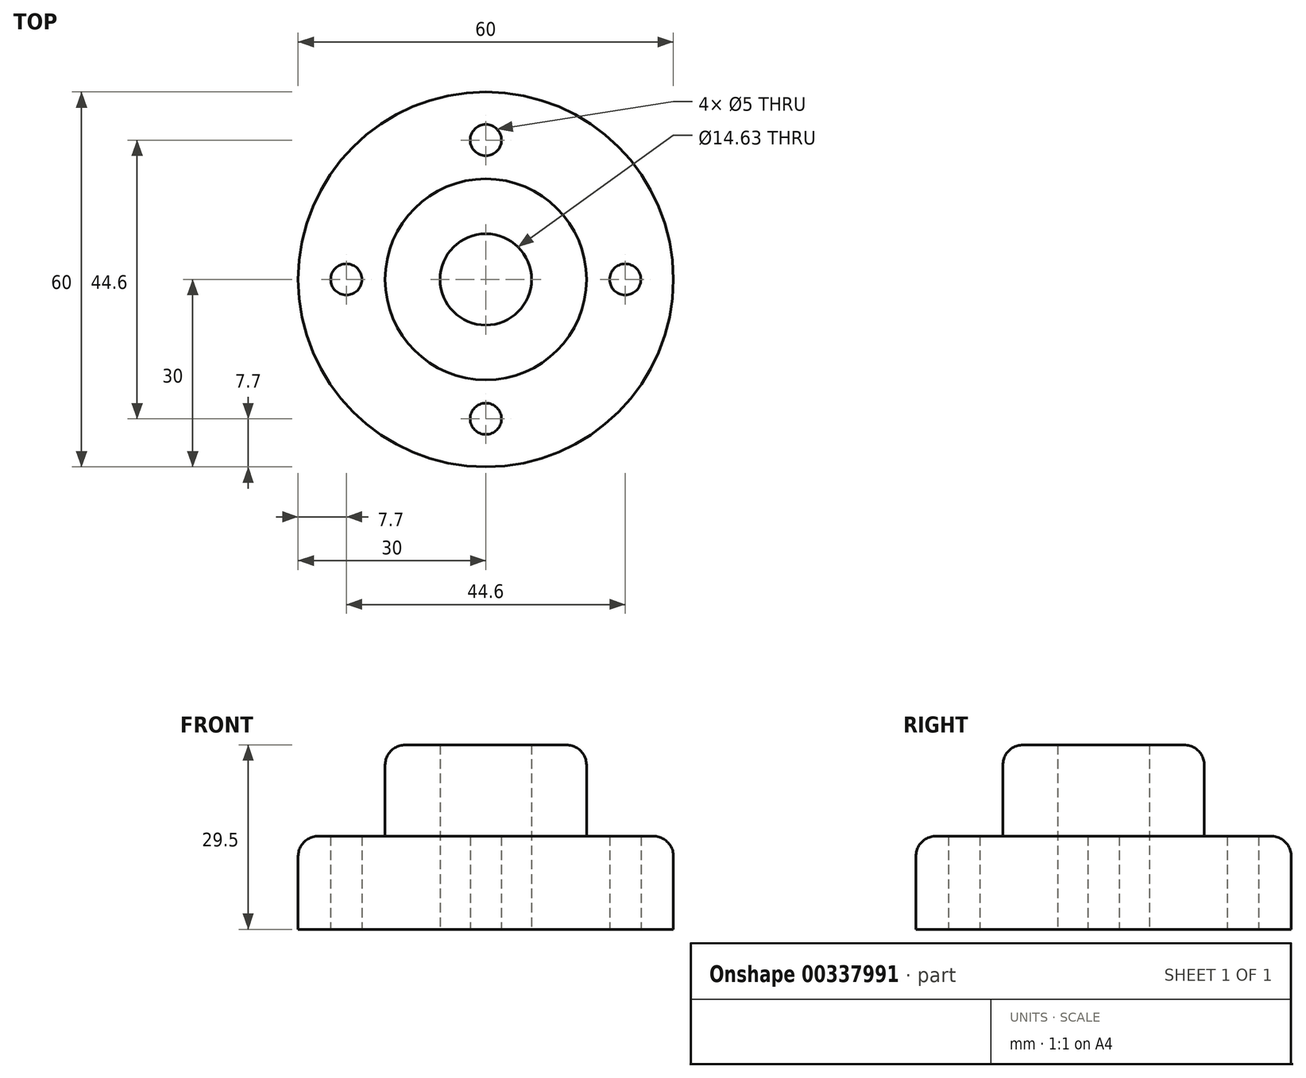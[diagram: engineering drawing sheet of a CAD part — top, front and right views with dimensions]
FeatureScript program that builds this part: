
annotation { "Feature Type Name" : "Feature", "Feature Type Description" : "" }
export const myFeature = defineFeature(function(context is Context, id is Id, definition is map)
    precondition{}
    {
        {
            var Q0;
            Q0=qCreatedBy(makeId("Top.planeOp"),FACE);
            var sketch = newSketch(context, id + "F0", { "sketchPlane" : qUnion([Q0])});
            skCircle(sketch, "E0", {"center": v(0, 0) * mm, "radius": 30 * mm});
            skCircle(sketch, "E1", {"center": v(0, 0) * mm, "radius": 16.1 * mm});
            skCircle(sketch, "E2", {"center": v(0, 0) * mm, "radius": 7.32 * mm});
            skCircle(sketch, "E3", {"center": v(0, 22.3) * mm, "radius": 2.5 * mm});
            skCircle(sketch, "E4", {"center": v(22.3, 0) * mm, "radius": 2.5 * mm});
            skCircle(sketch, "E5", {"center": v(0, -22.3) * mm, "radius": 2.5 * mm});
            skCircle(sketch, "E6", {"center": v(-22.3, 0) * mm, "radius": 2.5 * mm});
            skSolve(sketch);
        }
        {
            var Q0;
            Q0=makeQuery(id+"F0.imprint","IMPRINT",FACE,{"disambiguationData":[TD([[makeQuery(id+"F0.imprint","IMPRINT",EDGE,{"derivedFrom":sQuery(id+"F0.wireOp",EDGE,"E0")}),1.0]])]});
            extrude(context, id + "F1", {"entities" : qUnion([Q0]), "depth" : 14.9 * mm});
        }
        {
            var Q0;
            Q0=makeQuery(id+"F1.opExtrude","CAP_EDGE",EDGE,{"disambiguationData":[OSD([sQuery(id+"F0.wireOp",EDGE,"E0")])],"isStart":false});
            fillet(context, id + "F2", {"entities" : qUnion([Q0]), "radius" : 3.2 * mm, "tangentPropagation" : true, "allowEdgeOverflow" : false});
        }
        {
            var Q0;
            Q0=makeQuery(id+"F0.imprint","IMPRINT",FACE,{"disambiguationData":[TD([[makeQuery(id+"F0.imprint","IMPRINT",EDGE,{"derivedFrom":sQuery(id+"F0.wireOp",EDGE,"E1")}),1.0]])]});
            extrude(context, id + "F3", {"entities" : qUnion([Q0]), "operationType" : NewBodyOperationType.ADD, "depth" : 29.5 * mm});
        }
        {
            var Q0;
            Q0=makeQuery(id+"F3.opExtrude","CAP_EDGE",EDGE,{"disambiguationData":[OSD([sQuery(id+"F0.wireOp",EDGE,"E1")])],"isStart":false});
            fillet(context, id + "F4", {"entities" : qUnion([Q0]), "radius" : 3.2 * mm, "tangentPropagation" : true, "allowEdgeOverflow" : false});
        }
    });
